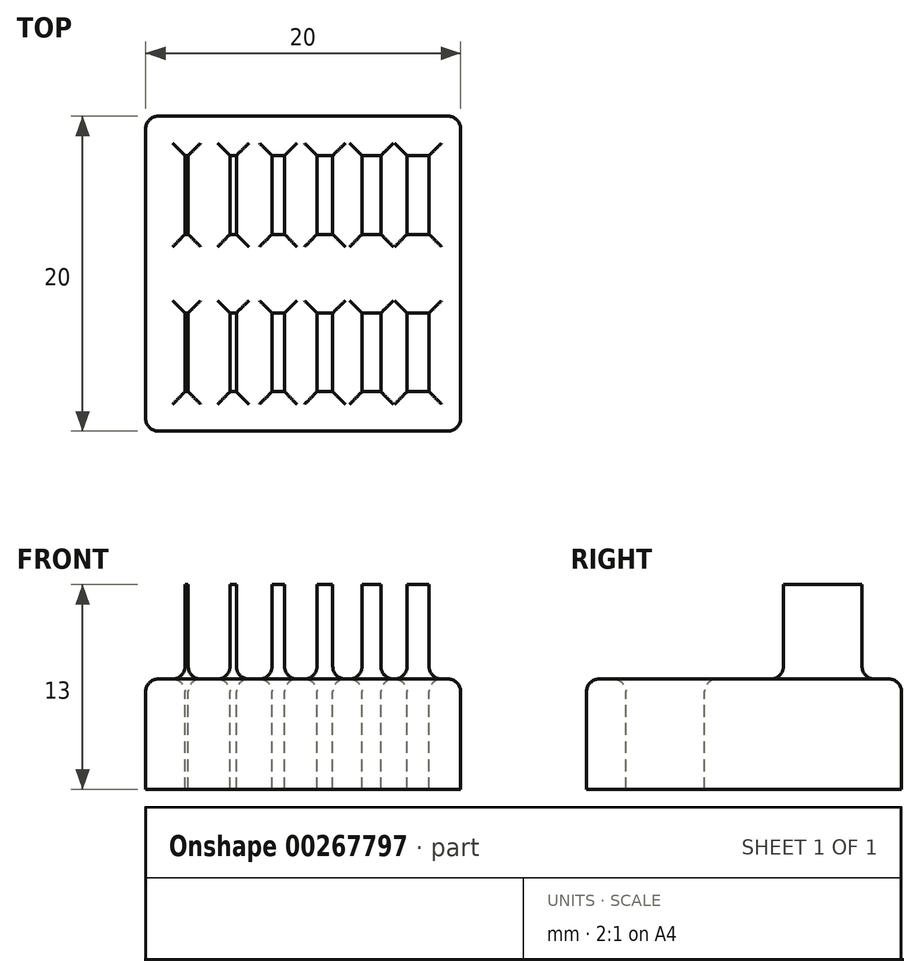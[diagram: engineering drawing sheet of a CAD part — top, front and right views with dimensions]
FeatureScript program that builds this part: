
annotation { "Feature Type Name" : "Feature", "Feature Type Description" : "" }
export const myFeature = defineFeature(function(context is Context, id is Id, definition is map)
    precondition{}
    {
        {
            var Q0;
            Q0=qCreatedBy(makeId("Top.planeOp"),FACE);
            var sketch = newSketch(context, id + "F0", { "sketchPlane" : qUnion([Q0])});
            skLineSegment(sketch, "E0.bottom", {"start": v(10, 10) * mm, "end": v(-10, 10) * mm});
            skLineSegment(sketch, "E0.top", {"start": v(10, -10) * mm, "end": v(-10, -10) * mm});
            skLineSegment(sketch, "E0.left", {"start": v(10, 10) * mm, "end": v(10, -10) * mm});
            skLineSegment(sketch, "E0.right", {"start": v(-10, 10) * mm, "end": v(-10, -10) * mm});
            skPoint(sketch, "E0.middle", {"position": v(0, 0) * mm});
            skSolve(sketch);
        }
        {
            var Q0;
            Q0=makeQuery(id+"F0.imprint","IMPRINT",FACE,{"disambiguationData":[TD([[makeQuery(id+"F0.imprint","IMPRINT",EDGE,{"derivedFrom":sQuery(id+"F0.wireOp",EDGE,"E0.bottom")}),1.0]])]});
            extrude(context, id + "F1", {"entities" : qUnion([Q0]), "depth" : 3 * mm});
        }
        {
            var Q0;
            Q0=makeQuery(id+"F1.opExtrude","CAP_FACE",FACE,{"disambiguationData":[OSD([sQuery(id+"F0.wireOp",EDGE,"E0.bottom"),sQuery(id+"F0.wireOp",EDGE,"E0.top"),sQuery(id+"F0.wireOp",EDGE,"E0.left"),sQuery(id+"F0.wireOp",EDGE,"E0.right")])],"isStart":false});
            var sketch = newSketch(context, id + "F2", { "sketchPlane" : qUnion([Q0])});
            skLineSegment(sketch, "E1.bottom", {"start": v(-7.5, 7.5) * mm, "end": v(-7.3, 7.5) * mm});
            skLineSegment(sketch, "E1.top", {"start": v(-7.5, 2.5) * mm, "end": v(-7.3, 2.5) * mm});
            skLineSegment(sketch, "E1.left", {"start": v(-7.5, 7.5) * mm, "end": v(-7.5, 2.5) * mm});
            skLineSegment(sketch, "E1.right", {"start": v(-7.3, 7.5) * mm, "end": v(-7.3, 2.5) * mm});
            skLineSegment(sketch, "E2.1.0.0", {"start": v(-4.34, 7.5) * mm, "end": v(-4.34, 2.5) * mm});
            skLineSegment(sketch, "E2.1.0.1", {"start": v(-4.54, 7.5) * mm, "end": v(-4.34, 7.5) * mm});
            skLineSegment(sketch, "E2.1.0.2", {"start": v(-4.54, 7.5) * mm, "end": v(-4.54, 2.5) * mm});
            skLineSegment(sketch, "E2.1.0.3", {"start": v(-4.54, 2.5) * mm, "end": v(-4.34, 2.5) * mm});
            skLineSegment(sketch, "E2.2.0.0", {"start": v(-1.38, 7.5) * mm, "end": v(-1.38, 2.5) * mm});
            skLineSegment(sketch, "E2.2.0.1", {"start": v(-1.58, 7.5) * mm, "end": v(-1.38, 7.5) * mm});
            skLineSegment(sketch, "E2.2.0.2", {"start": v(-1.58, 7.5) * mm, "end": v(-1.58, 2.5) * mm});
            skLineSegment(sketch, "E2.2.0.3", {"start": v(-1.58, 2.5) * mm, "end": v(-1.38, 2.5) * mm});
            skLineSegment(sketch, "E2.3.0.0", {"start": v(1.58, 7.5) * mm, "end": v(1.58, 2.5) * mm});
            skLineSegment(sketch, "E2.3.0.1", {"start": v(1.38, 7.5) * mm, "end": v(1.58, 7.5) * mm});
            skLineSegment(sketch, "E2.3.0.2", {"start": v(1.38, 7.5) * mm, "end": v(1.38, 2.5) * mm});
            skLineSegment(sketch, "E2.3.0.3", {"start": v(1.38, 2.5) * mm, "end": v(1.58, 2.5) * mm});
            skLineSegment(sketch, "E2.4.0.0", {"start": v(4.54, 7.5) * mm, "end": v(4.54, 2.5) * mm});
            skLineSegment(sketch, "E2.4.0.1", {"start": v(4.34, 7.5) * mm, "end": v(4.54, 7.5) * mm});
            skLineSegment(sketch, "E2.4.0.2", {"start": v(4.34, 7.5) * mm, "end": v(4.34, 2.5) * mm});
            skLineSegment(sketch, "E2.4.0.3", {"start": v(4.34, 2.5) * mm, "end": v(4.54, 2.5) * mm});
            skLineSegment(sketch, "E2.5.0.0", {"start": v(7.5, 7.5) * mm, "end": v(7.5, 2.5) * mm});
            skLineSegment(sketch, "E2.5.0.1", {"start": v(7.3, 7.5) * mm, "end": v(7.5, 7.5) * mm});
            skLineSegment(sketch, "E2.5.0.2", {"start": v(7.3, 7.5) * mm, "end": v(7.3, 2.5) * mm});
            skLineSegment(sketch, "E2.5.0.3", {"start": v(7.3, 2.5) * mm, "end": v(7.5, 2.5) * mm});
            skLineSegment(sketch, "E2.direction1", {"start": v(-7.3, 2.5) * mm, "end": v(-4.34, 2.5) * mm, "construction": true});
            skSolve(sketch);
        }
        {
            var Q0;
            Q0=makeQuery(id+"F2.imprint","IMPRINT",FACE,{"disambiguationData":[TD([[makeQuery(id+"F2.imprint","IMPRINT",EDGE,{"derivedFrom":sQuery(id+"F2.wireOp",EDGE,"E1.bottom")}),-1.0]])]});
            var Q1;
            Q1=makeQuery(id+"F2.imprint","IMPRINT",FACE,{"disambiguationData":[TD([[makeQuery(id+"F2.imprint","IMPRINT",EDGE,{"derivedFrom":sQuery(id+"F2.wireOp",EDGE,"E2.1.0.0")}),-1.0]])]});
            var Q2;
            Q2=makeQuery(id+"F2.imprint","IMPRINT",FACE,{"disambiguationData":[TD([[makeQuery(id+"F2.imprint","IMPRINT",EDGE,{"derivedFrom":sQuery(id+"F2.wireOp",EDGE,"E2.2.0.0")}),-1.0]])]});
            var Q3;
            Q3=makeQuery(id+"F2.imprint","IMPRINT",FACE,{"disambiguationData":[TD([[makeQuery(id+"F2.imprint","IMPRINT",EDGE,{"derivedFrom":sQuery(id+"F2.wireOp",EDGE,"E2.3.0.0")}),-1.0]])]});
            var Q4;
            Q4=makeQuery(id+"F2.imprint","IMPRINT",FACE,{"disambiguationData":[TD([[makeQuery(id+"F2.imprint","IMPRINT",EDGE,{"derivedFrom":sQuery(id+"F2.wireOp",EDGE,"E2.4.0.0")}),-1.0]])]});
            var Q5;
            Q5=makeQuery(id+"F2.imprint","IMPRINT",FACE,{"disambiguationData":[TD([[makeQuery(id+"F2.imprint","IMPRINT",EDGE,{"derivedFrom":sQuery(id+"F2.wireOp",EDGE,"E2.5.0.0")}),-1.0]])]});
            extrude(context, id + "F3", {"entities" : qUnion([Q0, Q1, Q2, Q3, Q4, Q5]), "operationType" : NewBodyOperationType.ADD, "depth" : 10 * mm});
        }
        {
            var Q0;
            Q0=makeQuery(id+"F3.opExtrude","SWEPT_FACE",FACE,{"disambiguationData":[OSD([sQuery(id+"F2.wireOp",EDGE,"E2.1.0.2")])]});
            var Q1;
            Q1=makeQuery(id+"F3.opExtrude","SWEPT_FACE",FACE,{"disambiguationData":[OSD([sQuery(id+"F2.wireOp",EDGE,"E2.1.0.0")])]});
            extrude(context, id + "F4", {"entities" : qUnion([Q0, Q1]), "operationType" : NewBodyOperationType.ADD, "endBound" : BoundingType.SYMMETRIC, "depth" : .2 * mm});
        }
        {
            var Q0;
            Q0=makeQuery(id+"F3.opExtrude","SWEPT_FACE",FACE,{"disambiguationData":[OSD([sQuery(id+"F2.wireOp",EDGE,"E2.2.0.2")])]});
            extrude(context, id + "F5", {"entities" : qUnion([Q0]), "operationType" : NewBodyOperationType.ADD, "endBound" : BoundingType.SYMMETRIC, "depth" : .8 * mm});
        }
        {
            var Q0;
            Q0=makeQuery(id+"F3.opExtrude","SWEPT_FACE",FACE,{"disambiguationData":[OSD([sQuery(id+"F2.wireOp",EDGE,"E2.3.0.2")])]});
            extrude(context, id + "F6", {"entities" : qUnion([Q0]), "operationType" : NewBodyOperationType.ADD, "endBound" : BoundingType.SYMMETRIC, "depth" : 1 * mm});
        }
        {
            var Q0;
            Q0=makeQuery(id+"F3.opExtrude","SWEPT_FACE",FACE,{"disambiguationData":[OSD([sQuery(id+"F2.wireOp",EDGE,"E2.4.0.2")])]});
            extrude(context, id + "F7", {"entities" : qUnion([Q0]), "operationType" : NewBodyOperationType.ADD, "endBound" : BoundingType.SYMMETRIC, "depth" : 1.2 * mm});
        }
        {
            var Q0;
            Q0=makeQuery(id+"F3.opExtrude","SWEPT_FACE",FACE,{"disambiguationData":[OSD([sQuery(id+"F2.wireOp",EDGE,"E2.5.0.2")])]});
            extrude(context, id + "F8", {"entities" : qUnion([Q0]), "operationType" : NewBodyOperationType.ADD, "endBound" : BoundingType.SYMMETRIC, "depth" : 1.4 * mm});
        }
        {
            var Q0;
            Q0=makeQuery(id+"F1.opExtrude","CAP_FACE",FACE,{"disambiguationData":[OSD([sQuery(id+"F0.wireOp",EDGE,"E0.bottom"),sQuery(id+"F0.wireOp",EDGE,"E0.top"),sQuery(id+"F0.wireOp",EDGE,"E0.left"),sQuery(id+"F0.wireOp",EDGE,"E0.right")])],"isStart":false});
            extrude(context, id + "F9", {"entities" : qUnion([Q0]), "operationType" : NewBodyOperationType.ADD, "depth" : 4 * mm});
        }
        {
            var Q0;
            Q0=makeQuery(id+"F9.opExtrude","CAP_FACE",FACE,{"disambiguationData":[OSD([sQuery(id+"F0.wireOp",EDGE,"E0.bottom"),sQuery(id+"F0.wireOp",EDGE,"E0.top"),sQuery(id+"F0.wireOp",EDGE,"E0.left"),sQuery(id+"F0.wireOp",EDGE,"E0.right")])],"isStart":false});
            var sketch = newSketch(context, id + "F10", { "sketchPlane" : qUnion([Q0])});
            skLineSegment(sketch, "E3", {"start": v(-7.3, -2.5) * mm, "end": v(-7.3, -7.5) * mm});
            skLineSegment(sketch, "E4", {"start": v(-7.3, -7.5) * mm, "end": v(-7.5, -7.5) * mm});
            skLineSegment(sketch, "E5", {"start": v(-7.5, -7.5) * mm, "end": v(-7.5, -2.5) * mm});
            skLineSegment(sketch, "E6", {"start": v(-7.5, -2.5) * mm, "end": v(-7.3, -2.5) * mm});
            skLineSegment(sketch, "E7", {"start": v(-4.64, -2.5) * mm, "end": v(-4.24, -2.5) * mm});
            skLineSegment(sketch, "E8", {"start": v(-4.24, -2.5) * mm, "end": v(-4.24, -7.5) * mm});
            skLineSegment(sketch, "E9", {"start": v(-4.24, -7.5) * mm, "end": v(-4.64, -7.5) * mm});
            skLineSegment(sketch, "E10", {"start": v(-4.64, -7.5) * mm, "end": v(-4.64, -2.5) * mm});
            skLineSegment(sketch, "E11", {"start": v(-1.18, -2.5) * mm, "end": v(-1.18, -7.5) * mm});
            skLineSegment(sketch, "E12", {"start": v(-1.18, -7.5) * mm, "end": v(-1.98, -7.5) * mm});
            skLineSegment(sketch, "E13", {"start": v(-1.98, -7.5) * mm, "end": v(-1.98, -2.5) * mm});
            skLineSegment(sketch, "E14", {"start": v(-1.98, -2.5) * mm, "end": v(-1.18, -2.5) * mm});
            skLineSegment(sketch, "E15", {"start": v(0.88, -2.5) * mm, "end": v(1.88, -2.5) * mm});
            skLineSegment(sketch, "E16", {"start": v(1.88, -2.5) * mm, "end": v(1.88, -7.5) * mm});
            skLineSegment(sketch, "E17", {"start": v(1.88, -7.5) * mm, "end": v(0.88, -7.5) * mm});
            skLineSegment(sketch, "E18", {"start": v(0.88, -7.5) * mm, "end": v(0.88, -2.5) * mm});
            skLineSegment(sketch, "E19", {"start": v(3.74, -2.5) * mm, "end": v(4.94, -2.5) * mm});
            skLineSegment(sketch, "E20", {"start": v(4.94, -2.5) * mm, "end": v(4.94, -7.5) * mm});
            skLineSegment(sketch, "E21", {"start": v(4.94, -7.5) * mm, "end": v(3.74, -7.5) * mm});
            skLineSegment(sketch, "E22", {"start": v(3.74, -7.5) * mm, "end": v(3.74, -2.5) * mm});
            skLineSegment(sketch, "E23", {"start": v(6.6, -2.5) * mm, "end": v(8, -2.5) * mm});
            skLineSegment(sketch, "E24", {"start": v(8, -2.5) * mm, "end": v(8, -7.5) * mm});
            skLineSegment(sketch, "E25", {"start": v(8, -7.5) * mm, "end": v(6.6, -7.5) * mm});
            skLineSegment(sketch, "E26", {"start": v(6.6, -7.5) * mm, "end": v(6.6, -2.5) * mm});
            skSolve(sketch);
        }
        {
            var Q0;
            Q0=makeQuery(id+"F10.imprint","IMPRINT",FACE,{"disambiguationData":[TD([[makeQuery(id+"F10.imprint","IMPRINT",EDGE,{"derivedFrom":sQuery(id+"F10.wireOp",EDGE,"E3")}),-1.0]])]});
            var Q1;
            Q1=makeQuery(id+"F10.imprint","IMPRINT",FACE,{"disambiguationData":[TD([[makeQuery(id+"F10.imprint","IMPRINT",EDGE,{"derivedFrom":sQuery(id+"F10.wireOp",EDGE,"E7")}),-1.0]])]});
            var Q2;
            Q2=makeQuery(id+"F10.imprint","IMPRINT",FACE,{"disambiguationData":[TD([[makeQuery(id+"F10.imprint","IMPRINT",EDGE,{"derivedFrom":sQuery(id+"F10.wireOp",EDGE,"E11")}),-1.0]])]});
            var Q3;
            Q3=makeQuery(id+"F10.imprint","IMPRINT",FACE,{"disambiguationData":[TD([[makeQuery(id+"F10.imprint","IMPRINT",EDGE,{"derivedFrom":sQuery(id+"F10.wireOp",EDGE,"E15")}),-1.0]])]});
            var Q4;
            Q4=makeQuery(id+"F10.imprint","IMPRINT",FACE,{"disambiguationData":[TD([[makeQuery(id+"F10.imprint","IMPRINT",EDGE,{"derivedFrom":sQuery(id+"F10.wireOp",EDGE,"E19")}),-1.0]])]});
            var Q5;
            Q5=makeQuery(id+"F10.imprint","IMPRINT",FACE,{"disambiguationData":[TD([[makeQuery(id+"F10.imprint","IMPRINT",EDGE,{"derivedFrom":sQuery(id+"F10.wireOp",EDGE,"E23")}),-1.0]])]});
            extrude(context, id + "F11", {"entities" : qUnion([Q0, Q1, Q2, Q3, Q4, Q5]), "operationType" : NewBodyOperationType.REMOVE, "endBound" : BoundingType.UP_TO_NEXT, "oppositeDirection" : true, "depth" : 25 * mm});
        }
        {
            var Q0;
            {var subQ0=sQuery(id+"F0.wireOp",EDGE,"E0.left");var subQ1=sQuery(id+"F0.wireOp",EDGE,"E0.top");Q0=makeQuery(id+"F9.boolean.opBoolean","MERGE",EDGE,{"derivedFrom":[makeQuery(id+"F1.opExtrude","SWEPT_EDGE",EDGE,{"disambiguationData":[OSD([subQ1,subQ0])]}),makeQuery(id+"F9.opExtrude","SWEPT_EDGE",EDGE,{"disambiguationData":[OSD([subQ1,subQ0])]})]});}
            var Q1;
            {var subQ0=sQuery(id+"F0.wireOp",EDGE,"E0.right");var subQ1=sQuery(id+"F0.wireOp",EDGE,"E0.top");Q1=makeQuery(id+"F9.boolean.opBoolean","MERGE",EDGE,{"derivedFrom":[makeQuery(id+"F1.opExtrude","SWEPT_EDGE",EDGE,{"disambiguationData":[OSD([subQ1,subQ0])]}),makeQuery(id+"F9.opExtrude","SWEPT_EDGE",EDGE,{"disambiguationData":[OSD([subQ1,subQ0])]})]});}
            var Q2;
            {var subQ0=sQuery(id+"F0.wireOp",EDGE,"E0.right");var subQ1=sQuery(id+"F0.wireOp",EDGE,"E0.bottom");Q2=makeQuery(id+"F9.boolean.opBoolean","MERGE",EDGE,{"derivedFrom":[makeQuery(id+"F1.opExtrude","SWEPT_EDGE",EDGE,{"disambiguationData":[OSD([subQ1,subQ0])]}),makeQuery(id+"F9.opExtrude","SWEPT_EDGE",EDGE,{"disambiguationData":[OSD([subQ1,subQ0])]})]});}
            var Q3;
            {var subQ0=sQuery(id+"F0.wireOp",EDGE,"E0.left");var subQ1=sQuery(id+"F0.wireOp",EDGE,"E0.bottom");Q3=makeQuery(id+"F9.boolean.opBoolean","MERGE",EDGE,{"derivedFrom":[makeQuery(id+"F1.opExtrude","SWEPT_EDGE",EDGE,{"disambiguationData":[OSD([subQ1,subQ0])]}),makeQuery(id+"F9.opExtrude","SWEPT_EDGE",EDGE,{"disambiguationData":[OSD([subQ1,subQ0])]})]});}
            var Q4;
            Q4=makeQuery(id+"F9.opExtrude","CAP_EDGE",EDGE,{"disambiguationData":[OSD([sQuery(id+"F0.wireOp",EDGE,"E0.right")])],"isStart":false});
            var Q5;
            Q5=makeQuery(id+"F9.opExtrude","CAP_EDGE",EDGE,{"disambiguationData":[OSD([sQuery(id+"F0.wireOp",EDGE,"E0.bottom")])],"isStart":false});
            var Q6;
            Q6=makeQuery(id+"F9.opExtrude","CAP_EDGE",EDGE,{"disambiguationData":[OSD([sQuery(id+"F0.wireOp",EDGE,"E0.top")])],"isStart":false});
            var Q7;
            Q7=makeQuery(id+"F9.opExtrude","CAP_EDGE",EDGE,{"disambiguationData":[OSD([sQuery(id+"F0.wireOp",EDGE,"E0.left")])],"isStart":false});
            var Q8;
            Q8=makeQuery(id+"F9.opExtrude","CAP_EDGE",EDGE,{"disambiguationData":[OSD([sQuery(id+"F2.wireOp",EDGE,"E1.left")])],"isStart":false});
            var Q9;
            Q9=makeQuery(id+"F9.opExtrude","CAP_EDGE",EDGE,{"disambiguationData":[OSD([sQuery(id+"F2.wireOp",EDGE,"E1.right")])],"isStart":false});
            var Q10;
            Q10=makeQuery(id+"F9.opExtrude","CAP_EDGE",EDGE,{"disambiguationData":[OSD([sQuery(id+"F2.wireOp",EDGE,"E2.1.0.2")])],"isStart":false});
            var Q11;
            Q11=makeQuery(id+"F9.opExtrude","CAP_EDGE",EDGE,{"disambiguationData":[OSD([sQuery(id+"F2.wireOp",EDGE,"E2.1.0.0")])],"isStart":false});
            var Q12;
            {var subQ0=sQuery(id+"F2.wireOp",EDGE,"E2.2.0.2");Q12=makeQuery(id+"F9.opExtrude","CAP_EDGE",EDGE,{"disambiguationData":[OSD([subQ0]),TDD([makeQuery(id+"F5.opExtrude","CAP_EDGE",EDGE,{"disambiguationData":[OSD([subQ0]),TDD([makeQuery(id+"F3.opExtrude","CAP_EDGE",EDGE,{"disambiguationData":[OSD([subQ0])],"isStart":true})])],"isStart":false})])],"isStart":false});}
            var Q13;
            {var subQ0=sQuery(id+"F2.wireOp",EDGE,"E2.2.0.2");Q13=makeQuery(id+"F9.opExtrude","CAP_EDGE",EDGE,{"disambiguationData":[OSD([subQ0]),TDD([makeQuery(id+"F5.opExtrude","CAP_EDGE",EDGE,{"disambiguationData":[OSD([subQ0]),TDD([makeQuery(id+"F3.opExtrude","CAP_EDGE",EDGE,{"disambiguationData":[OSD([subQ0])],"isStart":true})])],"isStart":true})])],"isStart":false});}
            var Q14;
            {var subQ0=sQuery(id+"F2.wireOp",EDGE,"E2.3.0.2");Q14=makeQuery(id+"F9.opExtrude","CAP_EDGE",EDGE,{"disambiguationData":[OSD([subQ0]),TDD([makeQuery(id+"F6.opExtrude","CAP_EDGE",EDGE,{"disambiguationData":[OSD([subQ0]),TDD([makeQuery(id+"F3.opExtrude","CAP_EDGE",EDGE,{"disambiguationData":[OSD([subQ0])],"isStart":true})])],"isStart":false})])],"isStart":false});}
            var Q15;
            {var subQ0=sQuery(id+"F2.wireOp",EDGE,"E2.3.0.2");Q15=makeQuery(id+"F9.opExtrude","CAP_EDGE",EDGE,{"disambiguationData":[OSD([subQ0]),TDD([makeQuery(id+"F6.opExtrude","CAP_EDGE",EDGE,{"disambiguationData":[OSD([subQ0]),TDD([makeQuery(id+"F3.opExtrude","CAP_EDGE",EDGE,{"disambiguationData":[OSD([subQ0])],"isStart":true})])],"isStart":true})])],"isStart":false});}
            var Q16;
            {var subQ0=sQuery(id+"F2.wireOp",EDGE,"E2.4.0.2");Q16=makeQuery(id+"F9.opExtrude","CAP_EDGE",EDGE,{"disambiguationData":[OSD([subQ0]),TDD([makeQuery(id+"F7.opExtrude","CAP_EDGE",EDGE,{"disambiguationData":[OSD([subQ0]),TDD([makeQuery(id+"F3.opExtrude","CAP_EDGE",EDGE,{"disambiguationData":[OSD([subQ0])],"isStart":true})])],"isStart":false})])],"isStart":false});}
            var Q17;
            {var subQ0=sQuery(id+"F2.wireOp",EDGE,"E2.5.0.2");Q17=makeQuery(id+"F9.opExtrude","CAP_EDGE",EDGE,{"disambiguationData":[OSD([subQ0]),TDD([makeQuery(id+"F8.opExtrude","CAP_EDGE",EDGE,{"disambiguationData":[OSD([subQ0]),TDD([makeQuery(id+"F3.opExtrude","CAP_EDGE",EDGE,{"disambiguationData":[OSD([subQ0])],"isStart":true})])],"isStart":false})])],"isStart":false});}
            var Q18;
            {var subQ0=sQuery(id+"F2.wireOp",EDGE,"E2.4.0.2");Q18=makeQuery(id+"F9.opExtrude","CAP_EDGE",EDGE,{"disambiguationData":[OSD([subQ0]),TDD([makeQuery(id+"F7.opExtrude","CAP_EDGE",EDGE,{"disambiguationData":[OSD([subQ0]),TDD([makeQuery(id+"F3.opExtrude","CAP_EDGE",EDGE,{"disambiguationData":[OSD([subQ0])],"isStart":true})])],"isStart":true})])],"isStart":false});}
            var Q19;
            {var subQ0=sQuery(id+"F2.wireOp",EDGE,"E2.5.0.2");Q19=makeQuery(id+"F9.opExtrude","CAP_EDGE",EDGE,{"disambiguationData":[OSD([subQ0]),TDD([makeQuery(id+"F8.opExtrude","CAP_EDGE",EDGE,{"disambiguationData":[OSD([subQ0]),TDD([makeQuery(id+"F3.opExtrude","CAP_EDGE",EDGE,{"disambiguationData":[OSD([subQ0])],"isStart":true})])],"isStart":true})])],"isStart":false});}
            var Q20;
            Q20=makeQuery(id+"F9.opExtrude","CAP_EDGE",EDGE,{"disambiguationData":[OSD([sQuery(id+"F2.wireOp",EDGE,"E1.bottom")])],"isStart":false});
            var Q21;
            Q21=makeQuery(id+"F9.opExtrude","CAP_EDGE",EDGE,{"disambiguationData":[OSD([sQuery(id+"F2.wireOp",EDGE,"E1.top")])],"isStart":false});
            var Q22;
            Q22=makeQuery(id+"F9.opExtrude","CAP_EDGE",EDGE,{"disambiguationData":[OSD([sQuery(id+"F2.wireOp",EDGE,"E2.1.0.0"),sQuery(id+"F2.wireOp",EDGE,"E2.1.0.2"),sQuery(id+"F2.wireOp",EDGE,"E2.1.0.3")])],"isStart":false});
            var Q23;
            Q23=makeQuery(id+"F9.opExtrude","CAP_EDGE",EDGE,{"disambiguationData":[OSD([sQuery(id+"F2.wireOp",EDGE,"E2.2.0.2"),sQuery(id+"F2.wireOp",EDGE,"E2.2.0.3")])],"isStart":false});
            var Q24;
            Q24=makeQuery(id+"F9.opExtrude","CAP_EDGE",EDGE,{"disambiguationData":[OSD([sQuery(id+"F2.wireOp",EDGE,"E2.3.0.2"),sQuery(id+"F2.wireOp",EDGE,"E2.3.0.3")])],"isStart":false});
            var Q25;
            Q25=makeQuery(id+"F9.opExtrude","CAP_EDGE",EDGE,{"disambiguationData":[OSD([sQuery(id+"F2.wireOp",EDGE,"E2.4.0.2"),sQuery(id+"F2.wireOp",EDGE,"E2.4.0.3")])],"isStart":false});
            var Q26;
            Q26=makeQuery(id+"F9.opExtrude","CAP_EDGE",EDGE,{"disambiguationData":[OSD([sQuery(id+"F2.wireOp",EDGE,"E2.5.0.2"),sQuery(id+"F2.wireOp",EDGE,"E2.5.0.3")])],"isStart":false});
            var Q27;
            Q27=makeQuery(id+"F11.boolean.opBoolean","COPY",EDGE,{"derivedFrom":makeQuery(id+"F11.opExtrude","CAP_EDGE",EDGE,{"disambiguationData":[OSD([sQuery(id+"F10.wireOp",EDGE,"E23")])],"isStart":true})});
            var Q28;
            Q28=makeQuery(id+"F11.boolean.opBoolean","COPY",EDGE,{"derivedFrom":makeQuery(id+"F11.opExtrude","CAP_EDGE",EDGE,{"disambiguationData":[OSD([sQuery(id+"F10.wireOp",EDGE,"E24")])],"isStart":true})});
            var Q29;
            Q29=makeQuery(id+"F11.boolean.opBoolean","COPY",EDGE,{"derivedFrom":makeQuery(id+"F11.opExtrude","CAP_EDGE",EDGE,{"disambiguationData":[OSD([sQuery(id+"F10.wireOp",EDGE,"E26")])],"isStart":true})});
            var Q30;
            Q30=makeQuery(id+"F11.boolean.opBoolean","COPY",EDGE,{"derivedFrom":makeQuery(id+"F11.opExtrude","CAP_EDGE",EDGE,{"disambiguationData":[OSD([sQuery(id+"F10.wireOp",EDGE,"E25")])],"isStart":true})});
            var Q31;
            Q31=makeQuery(id+"F11.boolean.opBoolean","COPY",EDGE,{"derivedFrom":makeQuery(id+"F11.opExtrude","CAP_EDGE",EDGE,{"disambiguationData":[OSD([sQuery(id+"F10.wireOp",EDGE,"E20")])],"isStart":true})});
            var Q32;
            Q32=makeQuery(id+"F11.boolean.opBoolean","COPY",EDGE,{"derivedFrom":makeQuery(id+"F11.opExtrude","CAP_EDGE",EDGE,{"disambiguationData":[OSD([sQuery(id+"F10.wireOp",EDGE,"E19")])],"isStart":true})});
            var Q33;
            Q33=makeQuery(id+"F11.boolean.opBoolean","COPY",EDGE,{"derivedFrom":makeQuery(id+"F11.opExtrude","CAP_EDGE",EDGE,{"disambiguationData":[OSD([sQuery(id+"F10.wireOp",EDGE,"E21")])],"isStart":true})});
            var Q34;
            Q34=makeQuery(id+"F11.boolean.opBoolean","COPY",EDGE,{"derivedFrom":makeQuery(id+"F11.opExtrude","CAP_EDGE",EDGE,{"disambiguationData":[OSD([sQuery(id+"F10.wireOp",EDGE,"E22")])],"isStart":true})});
            var Q35;
            Q35=makeQuery(id+"F11.boolean.opBoolean","COPY",EDGE,{"derivedFrom":makeQuery(id+"F11.opExtrude","CAP_EDGE",EDGE,{"disambiguationData":[OSD([sQuery(id+"F10.wireOp",EDGE,"E16")])],"isStart":true})});
            var Q36;
            Q36=makeQuery(id+"F11.boolean.opBoolean","COPY",EDGE,{"derivedFrom":makeQuery(id+"F11.opExtrude","CAP_EDGE",EDGE,{"disambiguationData":[OSD([sQuery(id+"F10.wireOp",EDGE,"E15")])],"isStart":true})});
            var Q37;
            Q37=makeQuery(id+"F11.boolean.opBoolean","COPY",EDGE,{"derivedFrom":makeQuery(id+"F11.opExtrude","CAP_EDGE",EDGE,{"disambiguationData":[OSD([sQuery(id+"F10.wireOp",EDGE,"E17")])],"isStart":true})});
            var Q38;
            Q38=makeQuery(id+"F11.boolean.opBoolean","COPY",EDGE,{"derivedFrom":makeQuery(id+"F11.opExtrude","CAP_EDGE",EDGE,{"disambiguationData":[OSD([sQuery(id+"F10.wireOp",EDGE,"E18")])],"isStart":true})});
            var Q39;
            Q39=makeQuery(id+"F11.boolean.opBoolean","COPY",EDGE,{"derivedFrom":makeQuery(id+"F11.opExtrude","CAP_EDGE",EDGE,{"disambiguationData":[OSD([sQuery(id+"F10.wireOp",EDGE,"E11")])],"isStart":true})});
            var Q40;
            Q40=makeQuery(id+"F11.boolean.opBoolean","COPY",EDGE,{"derivedFrom":makeQuery(id+"F11.opExtrude","CAP_EDGE",EDGE,{"disambiguationData":[OSD([sQuery(id+"F10.wireOp",EDGE,"E13")])],"isStart":true})});
            var Q41;
            Q41=makeQuery(id+"F11.boolean.opBoolean","COPY",EDGE,{"derivedFrom":makeQuery(id+"F11.opExtrude","CAP_EDGE",EDGE,{"disambiguationData":[OSD([sQuery(id+"F10.wireOp",EDGE,"E14")])],"isStart":true})});
            var Q42;
            Q42=makeQuery(id+"F11.boolean.opBoolean","COPY",EDGE,{"derivedFrom":makeQuery(id+"F11.opExtrude","CAP_EDGE",EDGE,{"disambiguationData":[OSD([sQuery(id+"F10.wireOp",EDGE,"E12")])],"isStart":true})});
            var Q43;
            Q43=makeQuery(id+"F11.boolean.opBoolean","COPY",EDGE,{"derivedFrom":makeQuery(id+"F11.opExtrude","CAP_EDGE",EDGE,{"disambiguationData":[OSD([sQuery(id+"F10.wireOp",EDGE,"E8")])],"isStart":true})});
            var Q44;
            Q44=makeQuery(id+"F11.boolean.opBoolean","COPY",EDGE,{"derivedFrom":makeQuery(id+"F11.opExtrude","CAP_EDGE",EDGE,{"disambiguationData":[OSD([sQuery(id+"F10.wireOp",EDGE,"E7")])],"isStart":true})});
            var Q45;
            Q45=makeQuery(id+"F11.boolean.opBoolean","COPY",EDGE,{"derivedFrom":makeQuery(id+"F11.opExtrude","CAP_EDGE",EDGE,{"disambiguationData":[OSD([sQuery(id+"F10.wireOp",EDGE,"E10")])],"isStart":true})});
            var Q46;
            Q46=makeQuery(id+"F11.boolean.opBoolean","COPY",EDGE,{"derivedFrom":makeQuery(id+"F11.opExtrude","CAP_EDGE",EDGE,{"disambiguationData":[OSD([sQuery(id+"F10.wireOp",EDGE,"E9")])],"isStart":true})});
            var Q47;
            Q47=makeQuery(id+"F11.boolean.opBoolean","COPY",EDGE,{"derivedFrom":makeQuery(id+"F11.opExtrude","CAP_EDGE",EDGE,{"disambiguationData":[OSD([sQuery(id+"F10.wireOp",EDGE,"E3")])],"isStart":true})});
            var Q48;
            Q48=makeQuery(id+"F11.boolean.opBoolean","COPY",EDGE,{"derivedFrom":makeQuery(id+"F11.opExtrude","CAP_EDGE",EDGE,{"disambiguationData":[OSD([sQuery(id+"F10.wireOp",EDGE,"E5")])],"isStart":true})});
            var Q49;
            Q49=makeQuery(id+"F9.opExtrude","CAP_FACE",FACE,{"disambiguationData":[OSD([sQuery(id+"F0.wireOp",EDGE,"E0.bottom"),sQuery(id+"F0.wireOp",EDGE,"E0.top"),sQuery(id+"F0.wireOp",EDGE,"E0.left"),sQuery(id+"F0.wireOp",EDGE,"E0.right")])],"isStart":false});
            fillet(context, id + "F12", {"entities" : qUnion([Q0, Q1, Q2, Q3, Q4, Q5, Q6, Q7, Q8, Q9, Q10, Q11, Q12, Q13, Q14, Q15, Q16, Q17, Q18, Q19, Q20, Q21, Q22, Q23, Q24, Q25, Q26, Q27, Q28, Q29, Q30, Q31, Q32, Q33, Q34, Q35, Q36, Q37, Q38, Q39, Q40, Q41, Q42, Q43, Q44, Q45, Q46, Q47, Q48, Q49]), "radius" : .8 * mm, "tangentPropagation" : true, "allowEdgeOverflow" : false});
        }
    });
